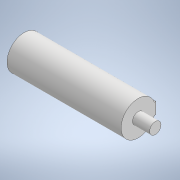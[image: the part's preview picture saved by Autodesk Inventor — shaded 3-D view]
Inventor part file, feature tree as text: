
AUTODESK INVENTOR PART (.ipt)
format: ipt  version: 2022.3 (Build 263350000, 350)  size: 114,688 bytes
history: native  units: mm
features: extrude x3, sketch x3, projected_geometry x1
ambient origin geometry x8: Origin, YZ Plane, XZ Plane, XY Plane, X Axis, Y Axis, Z Axis, Center Point
bodies: Solid1 (feature_tree)
feature tree (7):
  extrude  "Extrusion1"  Depth=20.0mm TaperAngle=0.0deg
  extrude  "Extrusion2"  Depth=3.0mm TaperAngle=0.0deg
  extrude  "Extrusion3"  Depth=2.0mm
  sketch  "Sketch1"  dims[d0=6.0mm d1=20.0mm d2=0.0mm]
  sketch  "Sketch2"  dims[d3=2.0mm d4=3.0mm d5=0.0mm]
  sketch  "Sketch3"  dims[d6=0.1mm d7=2.0mm d8=10.0mm d9=0.0mm]
  projected_geometry  "Projected Loop1"
